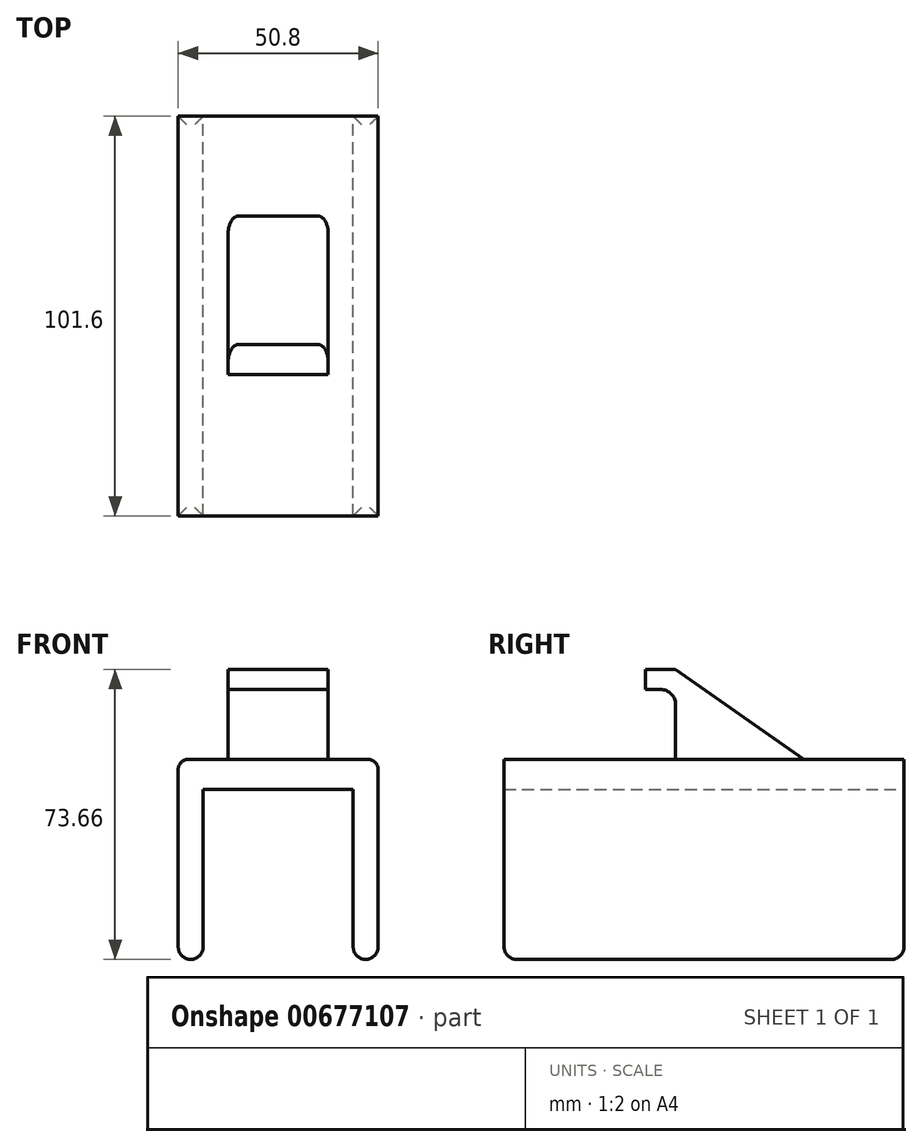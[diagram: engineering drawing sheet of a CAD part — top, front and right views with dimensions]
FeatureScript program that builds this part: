
annotation { "Feature Type Name" : "Feature", "Feature Type Description" : "" }
export const myFeature = defineFeature(function(context is Context, id is Id, definition is map)
    precondition{}
    {
        {
            var Q0;
            Q0=qCreatedBy(makeId("Front.planeOp"),FACE);
            var sketch = newSketch(context, id + "F0", { "sketchPlane" : qUnion([Q0])});
            skLineSegment(sketch, "E0.bottom", {"start": v(-25.4, -25.4) * mm, "end": v(-19.05, -25.4) * mm});
            skLineSegment(sketch, "E0.top", {"start": v(-25.4, 25.4) * mm, "end": v(25.4, 25.4) * mm});
            skLineSegment(sketch, "E0.left", {"start": v(-25.4, -25.4) * mm, "end": v(-25.4, 25.4) * mm});
            skLineSegment(sketch, "E0.right", {"start": v(25.4, -25.4) * mm, "end": v(25.4, 25.4) * mm});
            skLineSegment(sketch, "E1.top", {"start": v(-19.05, 17.78) * mm, "end": v(19.05, 17.78) * mm});
            skLineSegment(sketch, "E1.left", {"start": v(-19.05, -25.4) * mm, "end": v(-19.05, 17.78) * mm});
            skLineSegment(sketch, "E1.right", {"start": v(19.05, -25.4) * mm, "end": v(19.05, 17.78) * mm});
            skLineSegment(sketch, "E2.trimOffspring", {"start": v(19.05, -25.4) * mm, "end": v(25.4, -25.4) * mm});
            skSolve(sketch);
        }
        {
            var Q0;
            Q0 = qSketchRegion(id + "F0", true);
            extrude(context, id + "F1", {"entities" : qUnion([Q0]), "depth" : 101.6 * mm, "offsetDistance" : 25.4 * mm});
        }
        {
            var Q0;
            Q0=makeQuery(id+"F1.opExtrude","SWEPT_FACE",FACE,{"disambiguationData":[OSD([sQuery(id+"F0.wireOp",EDGE,"E0.bottom")])]});
            fillet(context, id + "F2", {"entities" : qUnion([Q0]), "radius" : 3.17 * mm, "tangentPropagation" : true, "allowEdgeOverflow" : false});
        }
        {
            var Q0;
            Q0=makeQuery(id+"F1.opExtrude","SWEPT_FACE",FACE,{"disambiguationData":[OSD([sQuery(id+"F0.wireOp",EDGE,"E2.trimOffspring")])]});
            fillet(context, id + "F3", {"entities" : qUnion([Q0]), "radius" : 3.17 * mm, "tangentPropagation" : true, "allowEdgeOverflow" : false});
        }
        {
            var Q0;
            Q0=qCreatedBy(makeId("Right.planeOp"),FACE);
            var sketch = newSketch(context, id + "F4", { "sketchPlane" : qUnion([Q0])});
            skLineSegment(sketch, "E3", {"start": v(-25.4, 25.4) * mm, "end": v(-58.05, 48.26) * mm});
            skLineSegment(sketch, "E4", {"start": v(-58.05, 43.18) * mm, "end": v(-58.05, 25.4) * mm});
            skLineSegment(sketch, "E5", {"start": v(-25.4, 25.4) * mm, "end": v(-58.05, 25.4) * mm});
            skLineSegment(sketch, "E6.bottom", {"start": v(-58.05, 43.18) * mm, "end": v(-65.67, 43.18) * mm});
            skLineSegment(sketch, "E6.top", {"start": v(-58.05, 48.26) * mm, "end": v(-65.67, 48.26) * mm});
            skLineSegment(sketch, "E7", {"start": v(-65.67, 48.26) * mm, "end": v(-65.67, 43.18) * mm});
            skSolve(sketch);
        }
        {
            var Q0;
            Q0 = qSketchRegion(id + "F4", true);
            extrude(context, id + "F5", {"entities" : qUnion([Q0]), "operationType" : NewBodyOperationType.ADD, "depth" : 12.7 * mm, "offsetDistance" : 25.4 * mm, "hasSecondDirection" : true, "secondDirectionOppositeDirection" : true, "secondDirectionDepth" : 12.7 * mm});
        }
        {
            var Q0;
            Q0=makeQuery(id+"F1.opExtrude","SWEPT_EDGE",EDGE,{"disambiguationData":[OSD([sQuery(id+"F0.wireOp",EDGE,"E0.top"),sQuery(id+"F0.wireOp",EDGE,"E0.right")])]});
            fillet(context, id + "F6", {"entities" : qUnion([Q0]), "radius" : 2.54 * mm, "tangentPropagation" : true, "allowEdgeOverflow" : false});
        }
        {
            var Q0;
            Q0=makeQuery(id+"F1.opExtrude","SWEPT_EDGE",EDGE,{"disambiguationData":[OSD([sQuery(id+"F0.wireOp",EDGE,"E0.top"),sQuery(id+"F0.wireOp",EDGE,"E0.left")])]});
            fillet(context, id + "F7", {"entities" : qUnion([Q0]), "radius" : 2.54 * mm, "tangentPropagation" : true, "allowEdgeOverflow" : false});
        }
        {
            var Q0;
            Q0=makeQuery(id+"F5.opExtrude","CAP_EDGE",EDGE,{"disambiguationData":[OSD([sQuery(id+"F4.wireOp",EDGE,"E3")])],"isStart":true});
            fillet(context, id + "F8", {"entities" : qUnion([Q0]), "radius" : 2.54 * mm, "tangentPropagation" : true, "allowEdgeOverflow" : false});
        }
        {
            var Q0;
            Q0=makeQuery(id+"F5.opExtrude","CAP_EDGE",EDGE,{"disambiguationData":[OSD([sQuery(id+"F4.wireOp",EDGE,"E3")])],"isStart":false});
            fillet(context, id + "F9", {"entities" : qUnion([Q0]), "radius" : 2.54 * mm, "tangentPropagation" : true, "allowEdgeOverflow" : false});
        }
        {
            var Q0;
            Q0=makeQuery(id+"F5.opExtrude","SWEPT_EDGE",EDGE,{"disambiguationData":[OSD([sQuery(id+"F4.wireOp",EDGE,"E4"),sQuery(id+"F4.wireOp",EDGE,"E6.bottom")])]});
            fillet(context, id + "F10", {"entities" : qUnion([Q0]), "radius" : 3.8 * mm, "tangentPropagation" : true, "allowEdgeOverflow" : false});
        }
    });
